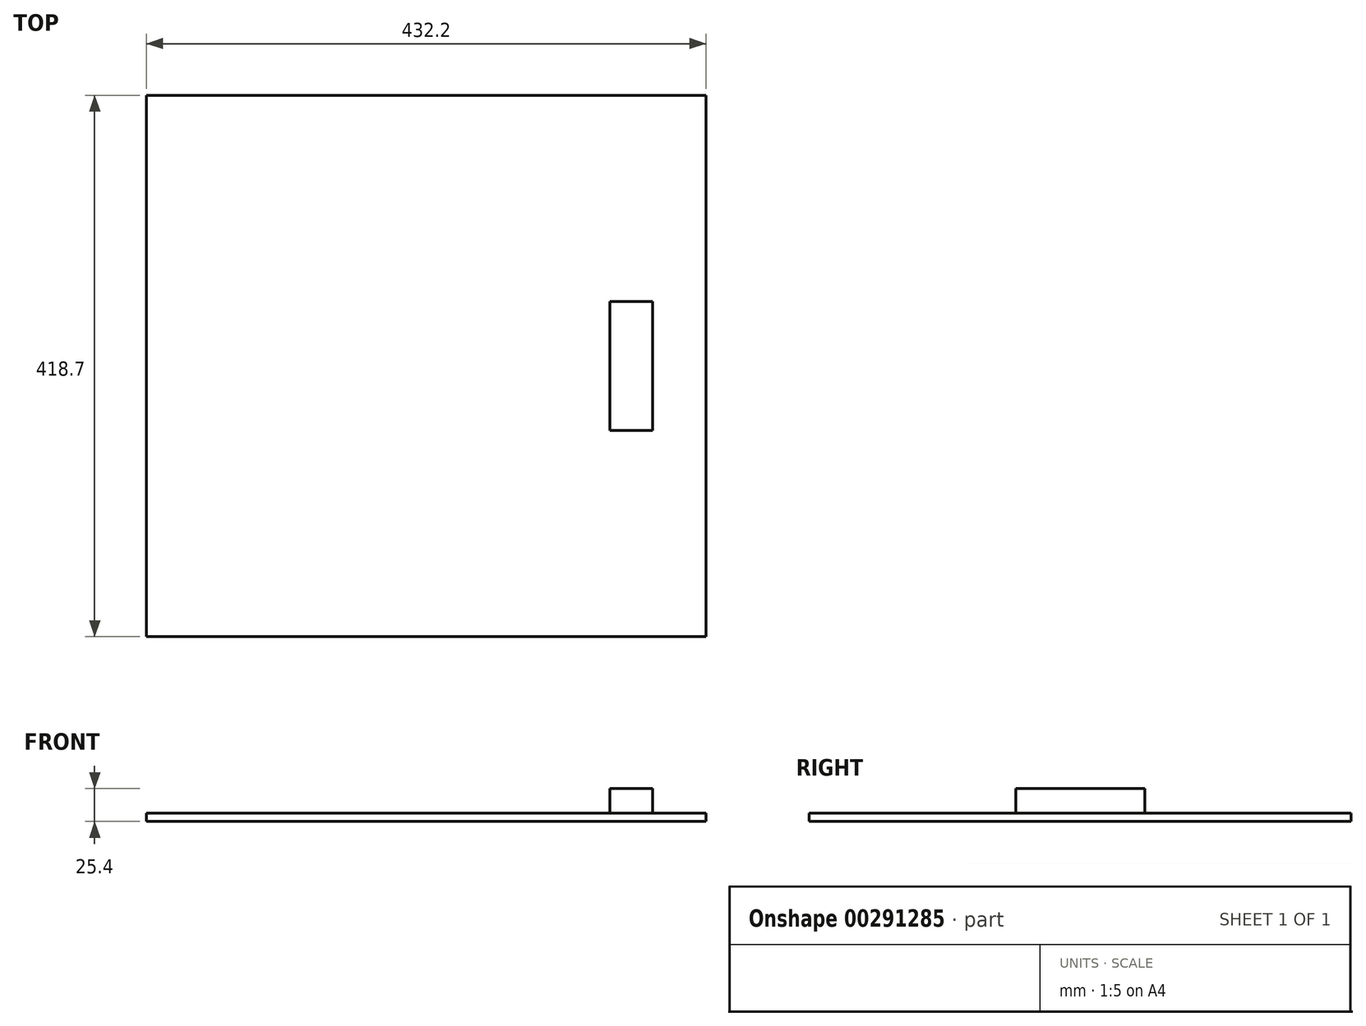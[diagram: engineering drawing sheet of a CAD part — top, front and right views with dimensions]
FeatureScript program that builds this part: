
annotation { "Feature Type Name" : "Feature", "Feature Type Description" : "" }
export const myFeature = defineFeature(function(context is Context, id is Id, definition is map)
    precondition{}
    {
        {
            var Q0;
            Q0=qCreatedBy(makeId("Top.planeOp"),FACE);
            var sketch = newSketch(context, id + "F0", { "sketchPlane" : qUnion([Q0])});
            skLineSegment(sketch, "E0.bottom", {"start": v(-216.1, 209.35) * mm, "end": v(216.1, 209.35) * mm});
            skLineSegment(sketch, "E0.top", {"start": v(-216.1, -209.35) * mm, "end": v(216.1, -209.35) * mm});
            skLineSegment(sketch, "E0.left", {"start": v(-216.1, 209.35) * mm, "end": v(-216.1, -209.35) * mm});
            skLineSegment(sketch, "E0.right", {"start": v(216.1, 209.35) * mm, "end": v(216.1, -209.35) * mm});
            skSolve(sketch);
        }
        {
            var Q0;
            Q0 = qSketchRegion(id + "F0", true);
            extrude(context, id + "F1", {"entities" : qUnion([Q0]), "depth" : 6.35 * mm});
        }
        {
            var Q0;
            Q0=qCreatedBy(makeId("Top.planeOp"),FACE);
            var sketch = newSketch(context, id + "F2", { "sketchPlane" : qUnion([Q0])});
            skLineSegment(sketch, "E1.bottom", {"start": v(175.1, -49.8) * mm, "end": v(142.1, -49.8) * mm});
            skLineSegment(sketch, "E1.top", {"start": v(175.1, 49.8) * mm, "end": v(142.1, 49.8) * mm});
            skLineSegment(sketch, "E1.left", {"start": v(175.1, -49.8) * mm, "end": v(175.1, 49.8) * mm});
            skLineSegment(sketch, "E1.right", {"start": v(142.1, -49.8) * mm, "end": v(142.1, 49.8) * mm});
            skPoint(sketch, "E1.middle", {"position": v(158.6, 0) * mm});
            skSolve(sketch);
        }
        {
            var Q0;
            Q0 = qSketchRegion(id + "F2", true);
            extrude(context, id + "F3", {"entities" : qUnion([Q0]), "operationType" : NewBodyOperationType.ADD, "depth" : 25.4 * mm});
        }
    });
